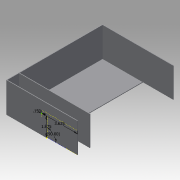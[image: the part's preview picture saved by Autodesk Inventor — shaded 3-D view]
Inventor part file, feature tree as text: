
AUTODESK INVENTOR PART (.ipt)
format: ipt  version: 2016 (Build 200138000, 138)  size: 135,168 bytes
history: native  units: in
note: dims shown in document units (in); Inventor stores cm internally (conversion verified against a paired STEP export)
features: sketch x6, extrude x4
ambient origin geometry x8: Origin, YZ Plane, XZ Plane, XY Plane, X Axis, Y Axis, Z Axis, Center Point
bodies: Solid1 (feature_tree)
feature tree (10):
  sketch  "Sketch1"  dims[d0=4.125in d1=9.8125in]
  extrude  "Extrusion1"  Depth=9.8125in
  extrude  "Extrusion2"  Depth=7.25in
  extrude  "Extrusion3"  Depth=7.25in
  extrude  "Extrusion4"  Depth=0.0625in
  sketch  "Sketch6"  dims[d12=3.0in d13=0.0in d14=1.25in d15=0.0625in d16=7.1875in d17=0.0in d18=2.0in d19=0.0in d20=1.875in d21=90.0deg d22=3.625in d23=0.15in]
  sketch  "Sketch2"  dims[d2=0.0625in d3=0.0in d6=7.25in]
  sketch  "Sketch3"  dims[d7=0.0625in d8=7.25in]
  sketch  "Sketch4"  dims[d9=0.0625in d10=0.0625in]
  sketch  "Sketch5"  dims[d11=12.0in]
